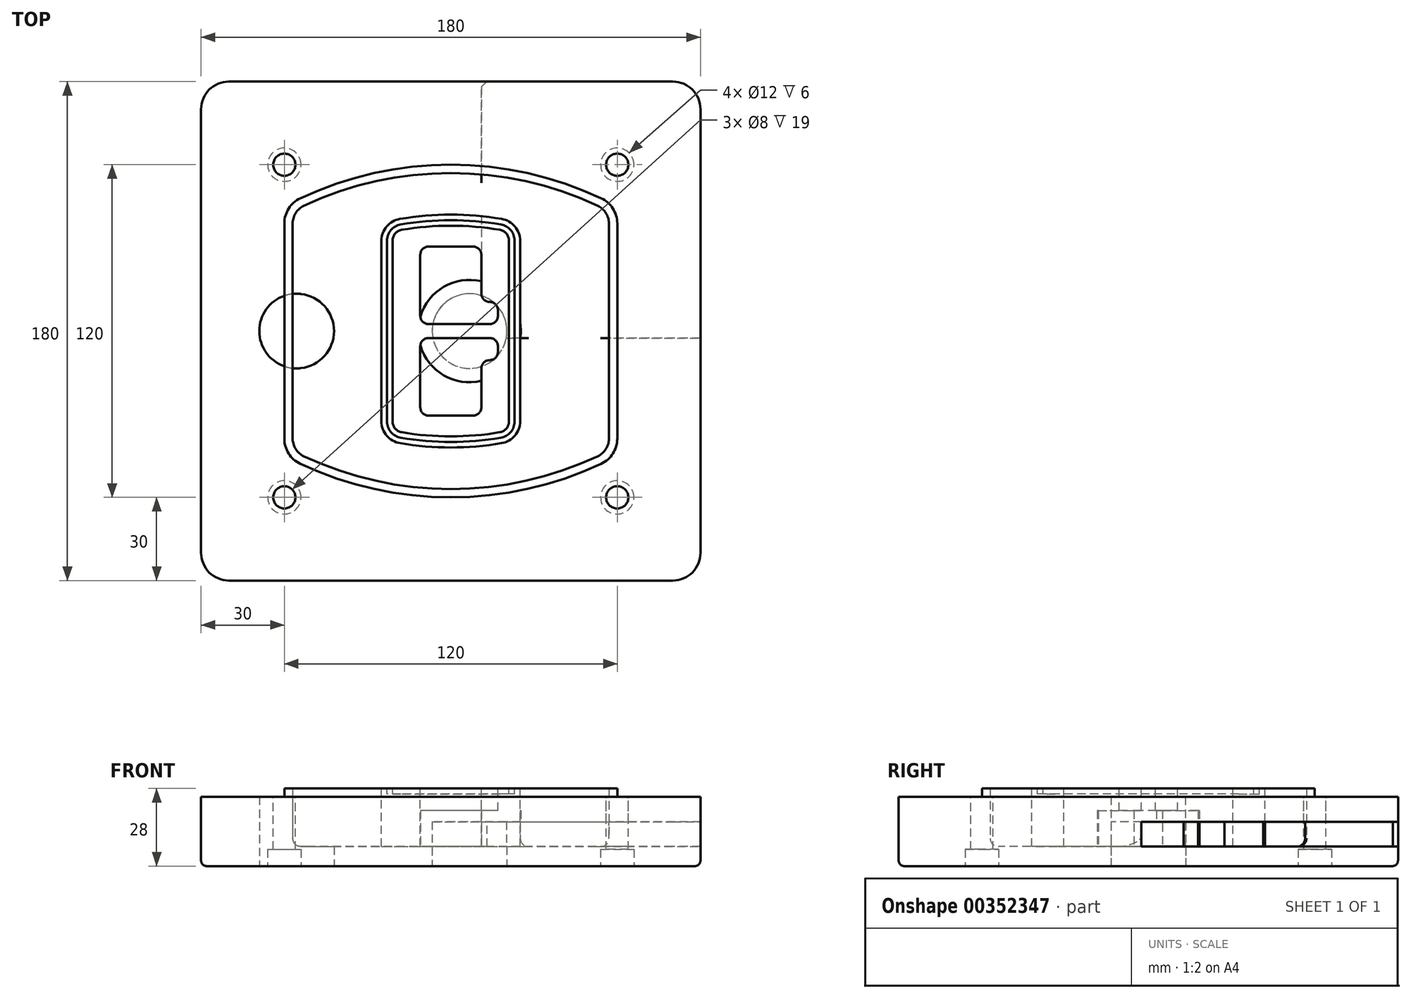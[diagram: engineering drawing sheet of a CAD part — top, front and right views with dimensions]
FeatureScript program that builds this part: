
annotation { "Feature Type Name" : "Feature", "Feature Type Description" : "" }
export const myFeature = defineFeature(function(context is Context, id is Id, definition is map)
    precondition{}
    {
        {
            var Q0;
            Q0=qCreatedBy(makeId("Top.planeOp"),FACE);
            var sketch = newSketch(context, id + "F0", { "sketchPlane" : qUnion([Q0])});
            skPoint(sketch, "E0.rect.middle", {"position": v(0, 0) * mm});
            skLineSegment(sketch, "E1.bottom", {"start": v(-80, -90) * mm, "end": v(80, -90) * mm});
            skLineSegment(sketch, "E1.top", {"start": v(-80, 90) * mm, "end": v(80, 90) * mm});
            skLineSegment(sketch, "E1.left", {"start": v(-90, -80) * mm, "end": v(-90, 80) * mm});
            skLineSegment(sketch, "E1.right", {"start": v(90, -80) * mm, "end": v(90, 80) * mm});
            skLineSegment(sketch, "E2", {"start": v(-90, 90) * mm, "end": v(90, -90) * mm, "construction": true});
            skLineSegment(sketch, "E3", {"start": v(90, 90) * mm, "end": v(-90, -90) * mm, "construction": true});
            skCircle(sketch, "E4", {"center": v(-60, 60) * mm, "radius": 4 * mm});
            skCircle(sketch, "E5", {"center": v(60, 60) * mm, "radius": 4 * mm});
            skCircle(sketch, "E6", {"center": v(60, -60) * mm, "radius": 4 * mm});
            skCircle(sketch, "E7", {"center": v(-60, -60) * mm, "radius": 4 * mm});
            skLineSegment(sketch, "E8", {"start": v(-60, 60) * mm, "end": v(60, 60) * mm, "construction": true});
            skLineSegment(sketch, "E9", {"start": v(60, 60) * mm, "end": v(60, -60) * mm, "construction": true});
            skLineSegment(sketch, "E10", {"start": v(60, -60) * mm, "end": v(-60, -60) * mm, "construction": true});
            skLineSegment(sketch, "E11", {"start": v(-60, -60) * mm, "end": v(-60, 60) * mm, "construction": true});
            skLineSegment(sketch, "E12", {"start": v(-60, 38.83) * mm, "end": v(-60, -38.83) * mm});
            skLineSegment(sketch, "E13", {"start": v(60, 38.83) * mm, "end": v(60, -38.83) * mm});
            skArc(sketch, "E14", {"start": v(54.26, 47.88) * mm, "mid": v(0, 60) * mm, "end": v(-54.26, 47.88) * mm});
            skArc(sketch, "E15", {"start": v(-54.26, -47.88) * mm, "mid": v(0, -60) * mm, "end": v(54.26, -47.88) * mm});
            skLineSegment(sketch, "E16", {"start": v(-60, 0) * mm, "end": v(60, 0) * mm, "construction": true});
            skPoint(sketch, "E17.visualSharp", {"position": v(-60, -45) * mm});
            skArc(sketch, "E17.filletArc", {"start": v(-60, -38.83) * mm, "mid": v(-58.44, -44.2) * mm, "end": v(-54.26, -47.88) * mm});
            skPoint(sketch, "E18.visualSharp", {"position": v(-60, 45) * mm});
            skArc(sketch, "E18.filletArc", {"start": v(-54.26, 47.88) * mm, "mid": v(-58.44, 44.2) * mm, "end": v(-60, 38.83) * mm});
            skPoint(sketch, "E19.visualSharp", {"position": v(60, 45) * mm});
            skArc(sketch, "E19.filletArc", {"start": v(60, 38.83) * mm, "mid": v(58.44, 44.2) * mm, "end": v(54.26, 47.88) * mm});
            skPoint(sketch, "E20.visualSharp", {"position": v(60, -45) * mm});
            skArc(sketch, "E20.filletArc", {"start": v(54.26, -47.88) * mm, "mid": v(58.44, -44.2) * mm, "end": v(60, -38.83) * mm});
            skPoint(sketch, "E21.visualSharp", {"position": v(-90, 90) * mm});
            skArc(sketch, "E21.filletArc", {"start": v(-80, 90) * mm, "mid": v(-87.07, 87.07) * mm, "end": v(-90, 80) * mm});
            skPoint(sketch, "E22.visualSharp", {"position": v(90, 90) * mm});
            skArc(sketch, "E22.filletArc", {"start": v(90, 80) * mm, "mid": v(87.07, 87.07) * mm, "end": v(80, 90) * mm});
            skPoint(sketch, "E23.visualSharp", {"position": v(90, -90) * mm});
            skArc(sketch, "E23.filletArc", {"start": v(80, -90) * mm, "mid": v(87.07, -87.07) * mm, "end": v(90, -80) * mm});
            skPoint(sketch, "E24.visualSharp", {"position": v(-90, -90) * mm});
            skArc(sketch, "E24.filletArc", {"start": v(-90, -80) * mm, "mid": v(-87.07, -87.07) * mm, "end": v(-80, -90) * mm});
            skArc(sketch, "E25.0", {"start": v(57, 38.83) * mm, "mid": v(55.9, 42.58) * mm, "end": v(52.98, 45.17) * mm});
            skLineSegment(sketch, "E25.1", {"start": v(57, 38.83) * mm, "end": v(57, -38.83) * mm});
            skArc(sketch, "E25.2", {"start": v(52.98, -45.17) * mm, "mid": v(55.9, -42.58) * mm, "end": v(57, -38.83) * mm});
            skArc(sketch, "E25.3", {"start": v(-52.98, -45.17) * mm, "mid": v(0, -57) * mm, "end": v(52.98, -45.17) * mm});
            skArc(sketch, "E25.4", {"start": v(-57, -38.83) * mm, "mid": v(-55.9, -42.58) * mm, "end": v(-52.98, -45.17) * mm});
            skArc(sketch, "E25.5", {"start": v(52.98, 45.17) * mm, "mid": v(0, 57) * mm, "end": v(-52.98, 45.17) * mm});
            skLineSegment(sketch, "E25.6", {"start": v(-57, 38.83) * mm, "end": v(-57, -38.83) * mm});
            skArc(sketch, "E25.7", {"start": v(-52.98, 45.17) * mm, "mid": v(-55.9, 42.58) * mm, "end": v(-57, 38.83) * mm});
            skArc(sketch, "E26.0", {"start": v(-55.96, 51.5) * mm, "mid": v(-61.82, 46.33) * mm, "end": v(-64, 38.83) * mm});
            skArc(sketch, "E26.1", {"start": v(55.96, 51.5) * mm, "mid": v(0, 64) * mm, "end": v(-55.96, 51.5) * mm});
            skArc(sketch, "E26.2", {"start": v(64, 38.83) * mm, "mid": v(61.82, 46.33) * mm, "end": v(55.96, 51.5) * mm});
            skLineSegment(sketch, "E26.3", {"start": v(64, 38.83) * mm, "end": v(64, -38.83) * mm});
            skArc(sketch, "E26.4", {"start": v(55.96, -51.5) * mm, "mid": v(61.82, -46.33) * mm, "end": v(64, -38.83) * mm});
            skLineSegment(sketch, "E26.5", {"start": v(-64, 38.83) * mm, "end": v(-64, -38.83) * mm});
            skArc(sketch, "E26.6", {"start": v(-55.96, -51.5) * mm, "mid": v(0, -64) * mm, "end": v(55.96, -51.5) * mm});
            skArc(sketch, "E26.7", {"start": v(-64, -38.83) * mm, "mid": v(-61.82, -46.33) * mm, "end": v(-55.96, -51.5) * mm});
            skSolve(sketch);
        }
        {
            var Q0;
            Q0=makeQuery(id+"F0.imprint","IMPRINT",FACE,{"disambiguationData":[TD([[makeQuery(id+"F0.imprint","IMPRINT",EDGE,{"derivedFrom":sQuery(id+"F0.wireOp",EDGE,"E1.bottom")}),1.0]])]});
            var Q1;
            Q1=makeQuery(id+"F0.imprint","IMPRINT",FACE,{"disambiguationData":[TD([[makeQuery(id+"F0.imprint","IMPRINT",EDGE,{"derivedFrom":sQuery(id+"F0.wireOp",EDGE,"E12")}),1.0]])]});
            var Q2;
            Q2=makeQuery(id+"F0.imprint","IMPRINT",FACE,{"disambiguationData":[TD([[makeQuery(id+"F0.imprint","IMPRINT",EDGE,{"derivedFrom":sQuery(id+"F0.wireOp",EDGE,"E25.0")}),1.0]])]});
            var Q3;
            Q3=makeQuery(id+"F0.imprint","IMPRINT",FACE,{"disambiguationData":[TD([[makeQuery(id+"F0.imprint","IMPRINT",EDGE,{"derivedFrom":sQuery(id+"F0.wireOp",EDGE,"E12")}),-1.0]])]});
            extrude(context, id + "F1", {"entities" : qUnion([Q0, Q1, Q2, Q3]), "oppositeDirection" : true, "depth" : 25 * mm});
        }
        {
            var Q0;
            Q0=makeQuery(id+"F0.imprint","IMPRINT",FACE,{"disambiguationData":[TD([[makeQuery(id+"F0.imprint","IMPRINT",EDGE,{"derivedFrom":sQuery(id+"F0.wireOp",EDGE,"E12")}),1.0]])]});
            extrude(context, id + "F2", {"entities" : qUnion([Q0]), "operationType" : NewBodyOperationType.ADD, "depth" : 3 * mm});
        }
        {
            var Q0;
            Q0=makeQuery(id+"F0.imprint","IMPRINT",FACE,{"disambiguationData":[TD([[makeQuery(id+"F0.imprint","IMPRINT",EDGE,{"derivedFrom":sQuery(id+"F0.wireOp",EDGE,"E25.0")}),1.0]])]});
            extrude(context, id + "F3", {"entities" : qUnion([Q0]), "operationType" : NewBodyOperationType.REMOVE, "oppositeDirection" : true, "depth" : 18 * mm});
        }
        {
            var Q0;
            Q0=makeQuery(id+"F2.opExtrude","CAP_FACE",FACE,{"disambiguationData":[OSD([sQuery(id+"F0.wireOp",EDGE,"E12"),sQuery(id+"F0.wireOp",EDGE,"E13"),sQuery(id+"F0.wireOp",EDGE,"E14"),sQuery(id+"F0.wireOp",EDGE,"E15"),sQuery(id+"F0.wireOp",EDGE,"E17.filletArc"),sQuery(id+"F0.wireOp",EDGE,"E18.filletArc"),sQuery(id+"F0.wireOp",EDGE,"E19.filletArc"),sQuery(id+"F0.wireOp",EDGE,"E20.filletArc"),sQuery(id+"F0.wireOp",EDGE,"E25.0"),sQuery(id+"F0.wireOp",EDGE,"E25.1"),sQuery(id+"F0.wireOp",EDGE,"E25.2"),sQuery(id+"F0.wireOp",EDGE,"E25.3"),sQuery(id+"F0.wireOp",EDGE,"E25.4"),sQuery(id+"F0.wireOp",EDGE,"E25.5"),sQuery(id+"F0.wireOp",EDGE,"E25.6"),sQuery(id+"F0.wireOp",EDGE,"E25.7")])],"isStart":false});
            var sketch = newSketch(context, id + "F4", { "sketchPlane" : qUnion([Q0])});
            skArc(sketch, "E27.0", {"start": v(-18.34, -40.45) * mm, "mid": v(0, -42) * mm, "end": v(18.34, -40.45) * mm});
            skArc(sketch, "E28.0", {"start": v(18.34, 40.45) * mm, "mid": v(0, 42) * mm, "end": v(-18.34, 40.45) * mm});
            skLineSegment(sketch, "E29", {"start": v(-25, 32.57) * mm, "end": v(-25, -32.57) * mm});
            skLineSegment(sketch, "E30", {"start": v(25, 32.57) * mm, "end": v(25, -32.57) * mm});
            skLineSegment(sketch, "E31", {"start": v(-25, 39.1) * mm, "end": v(25, 39.1) * mm, "construction": true});
            skLineSegment(sketch, "E32", {"start": v(-25, -39.1) * mm, "end": v(25, -39.1) * mm, "construction": true});
            skPoint(sketch, "E33.visualSharp", {"position": v(-25, 39.1) * mm});
            skArc(sketch, "E33.filletArc", {"start": v(-18.34, 40.45) * mm, "mid": v(-23.11, 37.73) * mm, "end": v(-25, 32.57) * mm});
            skPoint(sketch, "E34.visualSharp", {"position": v(25, 39.1) * mm});
            skArc(sketch, "E34.filletArc", {"start": v(25, 32.57) * mm, "mid": v(23.11, 37.73) * mm, "end": v(18.34, 40.45) * mm});
            skPoint(sketch, "E35.visualSharp", {"position": v(25, -39.1) * mm});
            skArc(sketch, "E35.filletArc", {"start": v(18.34, -40.45) * mm, "mid": v(23.11, -37.73) * mm, "end": v(25, -32.57) * mm});
            skPoint(sketch, "E36.visualSharp", {"position": v(-25, -39.1) * mm});
            skArc(sketch, "E36.filletArc", {"start": v(-25, -32.57) * mm, "mid": v(-23.11, -37.73) * mm, "end": v(-18.34, -40.45) * mm});
            skArc(sketch, "E37.0", {"start": v(52.98, 45.17) * mm, "mid": v(0, 57) * mm, "end": v(-52.98, 45.17) * mm});
            skArc(sketch, "E37.1", {"start": v(-52.98, 45.17) * mm, "mid": v(-55.9, 42.58) * mm, "end": v(-57, 38.83) * mm});
            skLineSegment(sketch, "E37.2", {"start": v(-57, 38.83) * mm, "end": v(-57, -38.83) * mm});
            skArc(sketch, "E37.3", {"start": v(-57, -38.83) * mm, "mid": v(-55.9, -42.58) * mm, "end": v(-52.98, -45.17) * mm});
            skArc(sketch, "E37.4", {"start": v(-52.98, -45.17) * mm, "mid": v(0, -57) * mm, "end": v(52.98, -45.17) * mm});
            skArc(sketch, "E37.5", {"start": v(52.98, -45.17) * mm, "mid": v(55.9, -42.58) * mm, "end": v(57, -38.83) * mm});
            skLineSegment(sketch, "E37.6", {"start": v(57, 38.83) * mm, "end": v(57, -38.83) * mm});
            skArc(sketch, "E37.7", {"start": v(57, 38.83) * mm, "mid": v(55.9, 42.58) * mm, "end": v(52.98, 45.17) * mm});
            skLineSegment(sketch, "E38.0", {"start": v(23, 32.57) * mm, "end": v(23, -32.57) * mm});
            skArc(sketch, "E38.1", {"start": v(18, -38.48) * mm, "mid": v(21.58, -36.44) * mm, "end": v(23, -32.57) * mm});
            skArc(sketch, "E38.2", {"start": v(-18, -38.48) * mm, "mid": v(0, -40) * mm, "end": v(18, -38.48) * mm});
            skArc(sketch, "E38.3", {"start": v(-23, -32.57) * mm, "mid": v(-21.58, -36.44) * mm, "end": v(-18, -38.48) * mm});
            skLineSegment(sketch, "E38.4", {"start": v(-23, 32.57) * mm, "end": v(-23, -32.57) * mm});
            skArc(sketch, "E38.5", {"start": v(23, 32.57) * mm, "mid": v(21.58, 36.44) * mm, "end": v(18, 38.48) * mm});
            skArc(sketch, "E38.6", {"start": v(-18, 38.48) * mm, "mid": v(-21.58, 36.44) * mm, "end": v(-23, 32.57) * mm});
            skArc(sketch, "E38.7", {"start": v(18, 38.48) * mm, "mid": v(0, 40) * mm, "end": v(-18, 38.48) * mm});
            skArc(sketch, "E39.0", {"start": v(21, 32.57) * mm, "mid": v(20.06, 35.15) * mm, "end": v(17.67, 36.5) * mm});
            skLineSegment(sketch, "E39.1", {"start": v(21, 32.57) * mm, "end": v(21, -32.57) * mm});
            skArc(sketch, "E39.2", {"start": v(17.67, -36.5) * mm, "mid": v(20.06, -35.15) * mm, "end": v(21, -32.57) * mm});
            skArc(sketch, "E39.3", {"start": v(-17.67, -36.5) * mm, "mid": v(0, -38) * mm, "end": v(17.67, -36.5) * mm});
            skArc(sketch, "E39.4", {"start": v(-21, -32.57) * mm, "mid": v(-20.06, -35.15) * mm, "end": v(-17.67, -36.5) * mm});
            skArc(sketch, "E39.5", {"start": v(17.67, 36.5) * mm, "mid": v(0, 38) * mm, "end": v(-17.67, 36.5) * mm});
            skLineSegment(sketch, "E39.6", {"start": v(-21, 32.57) * mm, "end": v(-21, -32.57) * mm});
            skArc(sketch, "E39.7", {"start": v(-17.67, 36.5) * mm, "mid": v(-20.06, 35.15) * mm, "end": v(-21, 32.57) * mm});
            skLineSegment(sketch, "E40", {"start": v(-25, 0) * mm, "end": v(25, 0) * mm, "construction": true});
            skLineSegment(sketch, "E41", {"start": v(-11, 5.5) * mm, "end": v(-11, 27.5) * mm});
            skLineSegment(sketch, "E42", {"start": v(-8, 30.5) * mm, "end": v(8, 30.5) * mm});
            skLineSegment(sketch, "E43", {"start": v(11, 27.5) * mm, "end": v(11, 13.5) * mm});
            skLineSegment(sketch, "E44", {"start": v(14, 10.5) * mm, "end": v(14, 10.5) * mm});
            skLineSegment(sketch, "E45", {"start": v(17, 7.5) * mm, "end": v(17, 5.5) * mm});
            skLineSegment(sketch, "E46", {"start": v(14, 2.5) * mm, "end": v(-8, 2.5) * mm});
            skPoint(sketch, "E47.visualSharp", {"position": v(-11, 30.5) * mm});
            skArc(sketch, "E47.filletArc", {"start": v(-8, 30.5) * mm, "mid": v(-10.12, 29.62) * mm, "end": v(-11, 27.5) * mm});
            skPoint(sketch, "E48.visualSharp", {"position": v(11, 30.5) * mm});
            skArc(sketch, "E48.filletArc", {"start": v(11, 27.5) * mm, "mid": v(10.12, 29.62) * mm, "end": v(8, 30.5) * mm});
            skPoint(sketch, "E49.visualSharp", {"position": v(11, 10.5) * mm});
            skArc(sketch, "E49.filletArc", {"start": v(11, 13.5) * mm, "mid": v(11.88, 11.38) * mm, "end": v(14, 10.5) * mm});
            skPoint(sketch, "E50.visualSharp", {"position": v(17, 10.5) * mm});
            skArc(sketch, "E50.filletArc", {"start": v(17, 7.5) * mm, "mid": v(16.12, 9.62) * mm, "end": v(14, 10.5) * mm});
            skPoint(sketch, "E51.visualSharp", {"position": v(17, 2.5) * mm});
            skArc(sketch, "E51.filletArc", {"start": v(14, 2.5) * mm, "mid": v(16.12, 3.38) * mm, "end": v(17, 5.5) * mm});
            skPoint(sketch, "E52.visualSharp", {"position": v(-11, 2.5) * mm});
            skArc(sketch, "E52.filletArc", {"start": v(-11, 5.5) * mm, "mid": v(-10.12, 3.38) * mm, "end": v(-8, 2.5) * mm});
            skLineSegment(sketch, "E53.0.MirrorCS", {"start": v(14, -2.5) * mm, "end": v(-8, -2.5) * mm});
            skArc(sketch, "E54.0.MirrorCS", {"start": v(-11, -5.5) * mm, "mid": v(-10.12, -3.38) * mm, "end": v(-8, -2.5) * mm});
            skLineSegment(sketch, "E55.0.MirrorCS", {"start": v(-11, -5.5) * mm, "end": v(-11, -27.5) * mm});
            skArc(sketch, "E56.0.MirrorCS", {"start": v(-8, -30.5) * mm, "mid": v(-10.12, -29.62) * mm, "end": v(-11, -27.5) * mm});
            skLineSegment(sketch, "E57.0.MirrorCS", {"start": v(-8, -30.5) * mm, "end": v(8, -30.5) * mm});
            skArc(sketch, "E58.0.MirrorCS", {"start": v(11, -27.5) * mm, "mid": v(10.12, -29.62) * mm, "end": v(8, -30.5) * mm});
            skLineSegment(sketch, "E59.0.MirrorCS", {"start": v(11, -27.5) * mm, "end": v(11, -13.5) * mm});
            skArc(sketch, "E60.0.MirrorCS", {"start": v(11, -13.5) * mm, "mid": v(11.88, -11.38) * mm, "end": v(14, -10.5) * mm});
            skArc(sketch, "E61.0.MirrorCS", {"start": v(17, -7.5) * mm, "mid": v(16.12, -9.62) * mm, "end": v(14, -10.5) * mm});
            skLineSegment(sketch, "E62.0.MirrorCS", {"start": v(17, -7.5) * mm, "end": v(17, -5.5) * mm});
            skArc(sketch, "E63.0.MirrorCS", {"start": v(14, -2.5) * mm, "mid": v(16.12, -3.38) * mm, "end": v(17, -5.5) * mm});
            skSolve(sketch);
        }
        {
            var Q0;
            Q0=makeQuery(id+"F4.imprint","IMPRINT",FACE,{"disambiguationData":[TD([[makeQuery(id+"F4.imprint","IMPRINT",EDGE,{"derivedFrom":sQuery(id+"F4.wireOp",EDGE,"E27.0")}),1.0]])]});
            var Q1;
            Q1=makeQuery(id+"F4.imprint","IMPRINT",FACE,{"disambiguationData":[TD([[makeQuery(id+"F4.imprint","IMPRINT",EDGE,{"derivedFrom":sQuery(id+"F4.wireOp",EDGE,"E38.0")}),-1.0]])]});
            var Q2;
            Q2=makeQuery(id+"F4.imprint","IMPRINT",FACE,{"disambiguationData":[TD([[makeQuery(id+"F4.imprint","IMPRINT",EDGE,{"derivedFrom":sQuery(id+"F4.wireOp",EDGE,"E39.0")}),1.0]])]});
            extrude(context, id + "F5", {"entities" : qUnion([Q0, Q1, Q2]), "operationType" : NewBodyOperationType.ADD, "endBound" : BoundingType.UP_TO_NEXT, "oppositeDirection" : true, "depth" : 25 * mm});
        }
        {
            var Q0;
            Q0=makeQuery(id+"F4.imprint","IMPRINT",FACE,{"disambiguationData":[TD([[makeQuery(id+"F4.imprint","IMPRINT",EDGE,{"derivedFrom":sQuery(id+"F4.wireOp",EDGE,"E38.0")}),-1.0]])]});
            extrude(context, id + "F6", {"entities" : qUnion([Q0]), "operationType" : NewBodyOperationType.REMOVE, "oppositeDirection" : true, "depth" : 2 * mm});
        }
        {
            var Q0;
            Q0=makeQuery(id+"F1.opExtrude","CAP_FACE",FACE,{"disambiguationData":[OSD([sQuery(id+"F0.wireOp",EDGE,"E1.bottom"),sQuery(id+"F0.wireOp",EDGE,"E1.top"),sQuery(id+"F0.wireOp",EDGE,"E1.left"),sQuery(id+"F0.wireOp",EDGE,"E1.right"),sQuery(id+"F0.wireOp",EDGE,"E4"),sQuery(id+"F0.wireOp",EDGE,"E5"),sQuery(id+"F0.wireOp",EDGE,"E6"),sQuery(id+"F0.wireOp",EDGE,"E7"),sQuery(id+"F0.wireOp",EDGE,"E21.filletArc"),sQuery(id+"F0.wireOp",EDGE,"E22.filletArc"),sQuery(id+"F0.wireOp",EDGE,"E23.filletArc"),sQuery(id+"F0.wireOp",EDGE,"E24.filletArc")])],"isStart":false});
            var sketch = newSketch(context, id + "F7", { "sketchPlane" : qUnion([Q0])});
            skCircle(sketch, "E64", {"center": v(6.76, 0) * mm, "radius": 13.47 * mm});
            skCircle(sketch, "E65", {"center": v(-55.56, 0) * mm, "radius": 13.47 * mm});
            skLineSegment(sketch, "E66", {"start": v(90, 0) * mm, "end": v(-90, 0) * mm});
            skCircle(sketch, "E67", {"center": v(6.76, 0) * mm, "radius": 18.47 * mm});
            skCircle(sketch, "E68", {"center": v(60, -60) * mm, "radius": 6 * mm});
            skCircle(sketch, "E69", {"center": v(-60, -60) * mm, "radius": 6 * mm});
            skCircle(sketch, "E70", {"center": v(-60, 60) * mm, "radius": 6 * mm});
            skCircle(sketch, "E71", {"center": v(60, 60) * mm, "radius": 6 * mm});
            skSolve(sketch);
        }
        {
            var Q0;
            {var subQ1=sQuery(id+"F7.wireOp",EDGE,"E66");var subQ4=sQuery(id+"F7.wireOp",EDGE,"E64");var subQ6=makeQuery(id+"F7.imprint","INTERSECT",VERTEX,{"disambiguationData":[OD(0.0)],"derivedFrom":[subQ4,subQ1]});Q0=makeQuery(id+"F7.imprint","IMPRINT",FACE,{"disambiguationData":[TD([[makeQuery(id+"F7.imprint","IMPRINT",EDGE,{"disambiguationData":[TD([[subQ6,-1.0]])],"derivedFrom":subQ4}),-1.0]])]});}
            var Q1;
            {var subQ0=sQuery(id+"F7.wireOp",EDGE,"E66");var subQ1=sQuery(id+"F7.wireOp",EDGE,"E64");var subQ3=makeQuery(id+"F7.imprint","INTERSECT",VERTEX,{"disambiguationData":[OD(0.0)],"derivedFrom":[subQ1,subQ0]});Q1=makeQuery(id+"F7.imprint","IMPRINT",FACE,{"disambiguationData":[TD([[makeQuery(id+"F7.imprint","IMPRINT",EDGE,{"disambiguationData":[TD([[subQ3,-1.0]])],"derivedFrom":subQ1}),1.0]])]});}
            var Q2;
            {var subQ0=sQuery(id+"F7.wireOp",EDGE,"E66");var subQ1=sQuery(id+"F7.wireOp",EDGE,"E64");var subQ3=makeQuery(id+"F7.imprint","INTERSECT",VERTEX,{"disambiguationData":[OD(0.0)],"derivedFrom":[subQ1,subQ0]});Q2=makeQuery(id+"F7.imprint","IMPRINT",FACE,{"disambiguationData":[TD([[makeQuery(id+"F7.imprint","IMPRINT",EDGE,{"disambiguationData":[TD([[subQ3,1.0]])],"derivedFrom":subQ1}),1.0]])]});}
            var Q3;
            {var subQ1=sQuery(id+"F7.wireOp",EDGE,"E66");var subQ4=sQuery(id+"F7.wireOp",EDGE,"E64");var subQ6=makeQuery(id+"F7.imprint","INTERSECT",VERTEX,{"disambiguationData":[OD(0.0)],"derivedFrom":[subQ4,subQ1]});Q3=makeQuery(id+"F7.imprint","IMPRINT",FACE,{"disambiguationData":[TD([[makeQuery(id+"F7.imprint","IMPRINT",EDGE,{"disambiguationData":[TD([[subQ6,1.0]])],"derivedFrom":subQ4}),-1.0]])]});}
            extrude(context, id + "F8", {"entities" : qUnion([Q0, Q1, Q2, Q3]), "operationType" : NewBodyOperationType.ADD, "oppositeDirection" : true, "depth" : 20 * mm});
        }
        {
            var Q0;
            {var subQ0=sQuery(id+"F7.wireOp",EDGE,"E66");var subQ1=sQuery(id+"F7.wireOp",EDGE,"E64");var subQ3=makeQuery(id+"F7.imprint","INTERSECT",VERTEX,{"disambiguationData":[OD(0.0)],"derivedFrom":[subQ1,subQ0]});Q0=makeQuery(id+"F7.imprint","IMPRINT",FACE,{"disambiguationData":[TD([[makeQuery(id+"F7.imprint","IMPRINT",EDGE,{"disambiguationData":[TD([[subQ3,-1.0]])],"derivedFrom":subQ1}),1.0]])]});}
            var Q1;
            {var subQ0=sQuery(id+"F7.wireOp",EDGE,"E66");var subQ1=sQuery(id+"F7.wireOp",EDGE,"E64");var subQ3=makeQuery(id+"F7.imprint","INTERSECT",VERTEX,{"disambiguationData":[OD(0.0)],"derivedFrom":[subQ1,subQ0]});Q1=makeQuery(id+"F7.imprint","IMPRINT",FACE,{"disambiguationData":[TD([[makeQuery(id+"F7.imprint","IMPRINT",EDGE,{"disambiguationData":[TD([[subQ3,1.0]])],"derivedFrom":subQ1}),1.0]])]});}
            extrude(context, id + "F9", {"entities" : qUnion([Q0, Q1]), "operationType" : NewBodyOperationType.REMOVE, "oppositeDirection" : true, "depth" : 16 * mm});
        }
        {
            var Q0;
            {var subQ0=sQuery(id+"F7.wireOp",EDGE,"E66");var subQ1=sQuery(id+"F7.wireOp",EDGE,"E65");var subQ3=makeQuery(id+"F7.imprint","INTERSECT",VERTEX,{"disambiguationData":[OD(0.0)],"derivedFrom":[subQ1,subQ0]});Q0=makeQuery(id+"F7.imprint","IMPRINT",FACE,{"disambiguationData":[TD([[makeQuery(id+"F7.imprint","IMPRINT",EDGE,{"disambiguationData":[TD([[subQ3,-1.0]])],"derivedFrom":subQ1}),1.0]])]});}
            var Q1;
            {var subQ0=sQuery(id+"F7.wireOp",EDGE,"E66");var subQ1=sQuery(id+"F7.wireOp",EDGE,"E65");var subQ3=makeQuery(id+"F7.imprint","INTERSECT",VERTEX,{"disambiguationData":[OD(0.0)],"derivedFrom":[subQ1,subQ0]});Q1=makeQuery(id+"F7.imprint","IMPRINT",FACE,{"disambiguationData":[TD([[makeQuery(id+"F7.imprint","IMPRINT",EDGE,{"disambiguationData":[TD([[subQ3,1.0]])],"derivedFrom":subQ1}),1.0]])]});}
            extrude(context, id + "F10", {"entities" : qUnion([Q0, Q1]), "operationType" : NewBodyOperationType.REMOVE, "oppositeDirection" : true, "depth" : 25 * mm});
        }
        {
            var Q0;
            Q0=makeQuery(id+"F7.imprint","IMPRINT",FACE,{"disambiguationData":[TD([[makeQuery(id+"F7.imprint","IMPRINT",EDGE,{"derivedFrom":sQuery(id+"F7.wireOp",EDGE,"E68")}),1.0]])]});
            var Q1;
            Q1=makeQuery(id+"F7.imprint","IMPRINT",FACE,{"disambiguationData":[TD([[makeQuery(id+"F7.imprint","IMPRINT",EDGE,{"derivedFrom":makeQuery(id+"F1.opExtrude","CAP_EDGE",EDGE,{"disambiguationData":[OSD([sQuery(id+"F0.wireOp",EDGE,"E5")])],"isStart":false})}),-1.0]])]});
            var Q2;
            Q2=makeQuery(id+"F7.imprint","IMPRINT",FACE,{"disambiguationData":[TD([[makeQuery(id+"F7.imprint","IMPRINT",EDGE,{"derivedFrom":sQuery(id+"F7.wireOp",EDGE,"E69")}),1.0]])]});
            var Q3;
            Q3=makeQuery(id+"F7.imprint","IMPRINT",FACE,{"disambiguationData":[TD([[makeQuery(id+"F7.imprint","IMPRINT",EDGE,{"derivedFrom":makeQuery(id+"F1.opExtrude","CAP_EDGE",EDGE,{"disambiguationData":[OSD([sQuery(id+"F0.wireOp",EDGE,"E4")])],"isStart":false})}),-1.0]])]});
            var Q4;
            Q4=makeQuery(id+"F7.imprint","IMPRINT",FACE,{"disambiguationData":[TD([[makeQuery(id+"F7.imprint","IMPRINT",EDGE,{"derivedFrom":sQuery(id+"F7.wireOp",EDGE,"E70")}),1.0]])]});
            var Q5;
            Q5=makeQuery(id+"F7.imprint","IMPRINT",FACE,{"disambiguationData":[TD([[makeQuery(id+"F7.imprint","IMPRINT",EDGE,{"derivedFrom":makeQuery(id+"F1.opExtrude","CAP_EDGE",EDGE,{"disambiguationData":[OSD([sQuery(id+"F0.wireOp",EDGE,"E7")])],"isStart":false})}),-1.0]])]});
            var Q6;
            Q6=makeQuery(id+"F7.imprint","IMPRINT",FACE,{"disambiguationData":[TD([[makeQuery(id+"F7.imprint","IMPRINT",EDGE,{"derivedFrom":sQuery(id+"F7.wireOp",EDGE,"E71")}),1.0]])]});
            var Q7;
            Q7=makeQuery(id+"F7.imprint","IMPRINT",FACE,{"disambiguationData":[TD([[makeQuery(id+"F7.imprint","IMPRINT",EDGE,{"derivedFrom":makeQuery(id+"F1.opExtrude","CAP_EDGE",EDGE,{"disambiguationData":[OSD([sQuery(id+"F0.wireOp",EDGE,"E6")])],"isStart":false})}),-1.0]])]});
            extrude(context, id + "F11", {"entities" : qUnion([Q0, Q1, Q2, Q3, Q4, Q5, Q6, Q7]), "operationType" : NewBodyOperationType.REMOVE, "oppositeDirection" : true, "depth" : 6 * mm});
        }
        {
            var Q0;
            Q0=makeQuery(id+"F9.boolean.opBoolean","COPY",FACE,{"derivedFrom":makeQuery(id+"F9.opExtrude","CAP_FACE",FACE,{"disambiguationData":[OSD([sQuery(id+"F7.wireOp",EDGE,"E64")])],"isStart":false})});
            var sketch = newSketch(context, id + "F12", { "sketchPlane" : qUnion([Q0])});
            skArc(sketch, "E72.0", {"start": v(11, -88.19) * mm, "mid": v(97.1, -83.6) * mm, "end": v(92.5, 2.5) * mm});
            skLineSegment(sketch, "E72.1", {"start": v(11, -17.97) * mm, "end": v(11, -17.97) * mm});
            skLineSegment(sketch, "E73", {"start": v(92.5, -105.13) * mm, "end": v(102.3, -105.13) * mm});
            skLineSegment(sketch, "E74.0", {"start": v(92.5, 2.5) * mm, "end": v(14, 2.5) * mm});
            skArc(sketch, "E74.1", {"start": v(14, 2.5) * mm, "mid": v(16.12, 3.38) * mm, "end": v(17, 5.5) * mm});
            skLineSegment(sketch, "E74.2", {"start": v(17, 7.5) * mm, "end": v(17, 5.5) * mm});
            skArc(sketch, "E74.3", {"start": v(17, 7.5) * mm, "mid": v(16.12, 9.62) * mm, "end": v(14, 10.5) * mm});
            skArc(sketch, "E74.4", {"start": v(11, 13.5) * mm, "mid": v(11.88, 11.38) * mm, "end": v(14, 10.5) * mm});
            skLineSegment(sketch, "E74.5", {"start": v(11, 13.5) * mm, "end": v(11, -88.19) * mm});
            skLineSegment(sketch, "E74.7", {"start": v(92.5, -2.5) * mm, "end": v(14, -2.5) * mm});
            skArc(sketch, "E74.8", {"start": v(14, -2.5) * mm, "mid": v(16.12, -3.38) * mm, "end": v(17, -5.5) * mm});
            skLineSegment(sketch, "E74.9", {"start": v(17, -7.5) * mm, "end": v(17, -5.5) * mm});
            skArc(sketch, "E74.10", {"start": v(17, -7.5) * mm, "mid": v(16.12, -9.62) * mm, "end": v(14, -10.5) * mm});
            skArc(sketch, "E74.11", {"start": v(11, -13.5) * mm, "mid": v(11.88, -11.38) * mm, "end": v(14, -10.5) * mm});
            skLineSegment(sketch, "E74.12", {"start": v(11, -17.97) * mm, "end": v(11, -13.5) * mm});
            skPoint(sketch, "E75.orphan", {"position": v(11, -27.5) * mm});
            skPoint(sketch, "E76.orphan", {"position": v(-8, -2.5) * mm});
            skPoint(sketch, "E77.orphan", {"position": v(-8, 2.5) * mm});
            skPoint(sketch, "E78.orphan", {"position": v(11, 27.5) * mm});
            skSolve(sketch);
        }
        {
            var Q0;
            {var subQ7=sQuery(id+"F12.wireOp",EDGE,"E72.0");var subQ14=sQuery(id+"F12.wireOp",EDGE,"E72.1");var subQ16=sQuery(id+"F12.wireOp",EDGE,"E74.1");var subQ18=sQuery(id+"F12.wireOp",EDGE,"E74.8");Q0=qUnion([makeQuery(id+"F12.imprint","IMPRINT",FACE,{"disambiguationData":[TD([[makeQuery(id+"F12.imprint","IMPRINT",EDGE,{"derivedFrom":subQ7}),1.0]])]}),makeQuery(id+"F12.imprint","IMPRINT",FACE,{"disambiguationData":[TD([[makeQuery(id+"F12.imprint","IMPRINT",EDGE,{"derivedFrom":subQ14}),1.0]])]}),makeQuery(id+"F12.imprint","IMPRINT",FACE,{"disambiguationData":[TD([[makeQuery(id+"F12.imprint","IMPRINT",EDGE,{"derivedFrom":subQ16}),1.0]])]}),makeQuery(id+"F12.imprint","IMPRINT",FACE,{"disambiguationData":[TD([[makeQuery(id+"F12.imprint","IMPRINT",EDGE,{"derivedFrom":subQ18}),-1.0]])]})]);}
            var Q1;
            Q1=makeQuery(id+"F5.boolean.opBoolean","SPLIT",FACE,{"disambiguationData":[TD([makeQuery(id+"F5.opExtrude","SWEPT_FACE",FACE,{"disambiguationData":[OSD([sQuery(id+"F4.wireOp",EDGE,"E41")])]})])],"derivedFrom":makeQuery(id+"F3.boolean.opBoolean","COPY",FACE,{"derivedFrom":makeQuery(id+"F3.opExtrude","CAP_FACE",FACE,{"disambiguationData":[OSD([sQuery(id+"F0.wireOp",EDGE,"E25.0"),sQuery(id+"F0.wireOp",EDGE,"E25.1"),sQuery(id+"F0.wireOp",EDGE,"E25.2"),sQuery(id+"F0.wireOp",EDGE,"E25.3"),sQuery(id+"F0.wireOp",EDGE,"E25.4"),sQuery(id+"F0.wireOp",EDGE,"E25.5"),sQuery(id+"F0.wireOp",EDGE,"E25.6"),sQuery(id+"F0.wireOp",EDGE,"E25.7")])],"isStart":false})})});
            extrude(context, id + "F13", {"entities" : qUnion([Q0]), "operationType" : NewBodyOperationType.REMOVE, "endBound" : BoundingType.UP_TO_SURFACE, "endBoundEntityFace" : qUnion([Q1]), "depth" : 25 * mm});
        }
        {
            var Q0;
            Q0=makeQuery(id+"F3.boolean.opBoolean","COPY",EDGE,{"derivedFrom":makeQuery(id+"F3.opExtrude","CAP_EDGE",EDGE,{"disambiguationData":[OSD([sQuery(id+"F0.wireOp",EDGE,"E25.6")])],"isStart":false})});
            var Q1;
            Q1=makeQuery(id+"F8.boolean.opBoolean","INTERSECT",EDGE,{"derivedFrom":[makeQuery(id+"F5.opExtrude","SWEPT_FACE",FACE,{"disambiguationData":[OSD([sQuery(id+"F4.wireOp",EDGE,"E30")])]}),makeQuery(id+"F8.opExtrude","CAP_FACE",FACE,{"disambiguationData":[OSD([sQuery(id+"F7.wireOp",EDGE,"E67")])],"isStart":false})]});
            var Q2;
            Q2=makeQuery(id+"F8.boolean.opBoolean","INTERSECT",EDGE,{"disambiguationData":[OD(1.0)],"derivedFrom":[makeQuery(id+"F5.opExtrude","SWEPT_FACE",FACE,{"disambiguationData":[OSD([sQuery(id+"F4.wireOp",EDGE,"E30")])]}),makeQuery(id+"F8.opExtrude","SWEPT_FACE",FACE,{"disambiguationData":[OSD([sQuery(id+"F7.wireOp",EDGE,"E67")])]})]});
            var Q3;
            {var subQ0=makeQuery(id+"F3.boolean.opBoolean","COPY",FACE,{"derivedFrom":makeQuery(id+"F3.opExtrude","CAP_FACE",FACE,{"disambiguationData":[OSD([sQuery(id+"F0.wireOp",EDGE,"E25.0"),sQuery(id+"F0.wireOp",EDGE,"E25.1"),sQuery(id+"F0.wireOp",EDGE,"E25.2"),sQuery(id+"F0.wireOp",EDGE,"E25.3"),sQuery(id+"F0.wireOp",EDGE,"E25.4"),sQuery(id+"F0.wireOp",EDGE,"E25.5"),sQuery(id+"F0.wireOp",EDGE,"E25.6"),sQuery(id+"F0.wireOp",EDGE,"E25.7")])],"isStart":false})});var subQ1=sQuery(id+"F4.wireOp",EDGE,"E30");Q3=makeQuery(id+"F8.boolean.opBoolean","SPLIT",EDGE,{"disambiguationData":[TD([makeQuery(id+"F5.opExtrude","SWEPT_FACE",FACE,{"disambiguationData":[OSD([sQuery(id+"F4.wireOp",EDGE,"E35.filletArc")])]})])],"derivedFrom":makeQuery(id+"F5.opExtrude","TWEAK_EDGE",EDGE,{"derivedFrom":[subQ0,makeQuery(id+"F4.imprint","IMPRINT",EDGE,{"derivedFrom":subQ1})]})});}
            var Q4;
            {var subQ0=sQuery(id+"F0.wireOp",EDGE,"E25.0");var subQ1=sQuery(id+"F0.wireOp",EDGE,"E25.1");var subQ2=sQuery(id+"F0.wireOp",EDGE,"E25.2");var subQ3=sQuery(id+"F0.wireOp",EDGE,"E25.3");var subQ4=sQuery(id+"F0.wireOp",EDGE,"E25.4");var subQ5=sQuery(id+"F0.wireOp",EDGE,"E25.5");var subQ6=sQuery(id+"F0.wireOp",EDGE,"E25.6");var subQ7=sQuery(id+"F0.wireOp",EDGE,"E25.7");Q4=makeQuery(id+"F8.boolean.opBoolean","INTERSECT",EDGE,{"derivedFrom":[makeQuery(id+"F5.boolean.opBoolean","SPLIT",FACE,{"disambiguationData":[TD([makeQuery(id+"F2.opExtrude","SWEPT_FACE",FACE,{"disambiguationData":[OSD([subQ0])]})])],"derivedFrom":makeQuery(id+"F3.boolean.opBoolean","COPY",FACE,{"derivedFrom":makeQuery(id+"F3.opExtrude","CAP_FACE",FACE,{"disambiguationData":[OSD([subQ0,subQ1,subQ2,subQ3,subQ4,subQ5,subQ6,subQ7])],"isStart":false})})}),makeQuery(id+"F8.opExtrude","SWEPT_FACE",FACE,{"disambiguationData":[OSD([sQuery(id+"F7.wireOp",EDGE,"E67")])]})]});}
            var Q5;
            Q5=makeQuery(id+"F8.boolean.opBoolean","INTERSECT",EDGE,{"disambiguationData":[OD(0.0)],"derivedFrom":[makeQuery(id+"F5.opExtrude","SWEPT_FACE",FACE,{"disambiguationData":[OSD([sQuery(id+"F4.wireOp",EDGE,"E30")])]}),makeQuery(id+"F8.opExtrude","SWEPT_FACE",FACE,{"disambiguationData":[OSD([sQuery(id+"F7.wireOp",EDGE,"E67")])]})]});
            fillet(context, id + "F14", {"entities" : qUnion([Q0, Q1, Q2, Q3, Q4, Q5]), "radius" : 3 * mm, "tangentPropagation" : true, "allowEdgeOverflow" : false});
        }
        {
            var Q0;
            Q0=makeQuery(id+"F1.opExtrude","CAP_EDGE",EDGE,{"disambiguationData":[OSD([sQuery(id+"F0.wireOp",EDGE,"E1.bottom")])],"isStart":false});
            fillet(context, id + "F15", {"entities" : qUnion([Q0]), "radius" : 2 * mm, "tangentPropagation" : true, "allowEdgeOverflow" : false});
        }
    });
